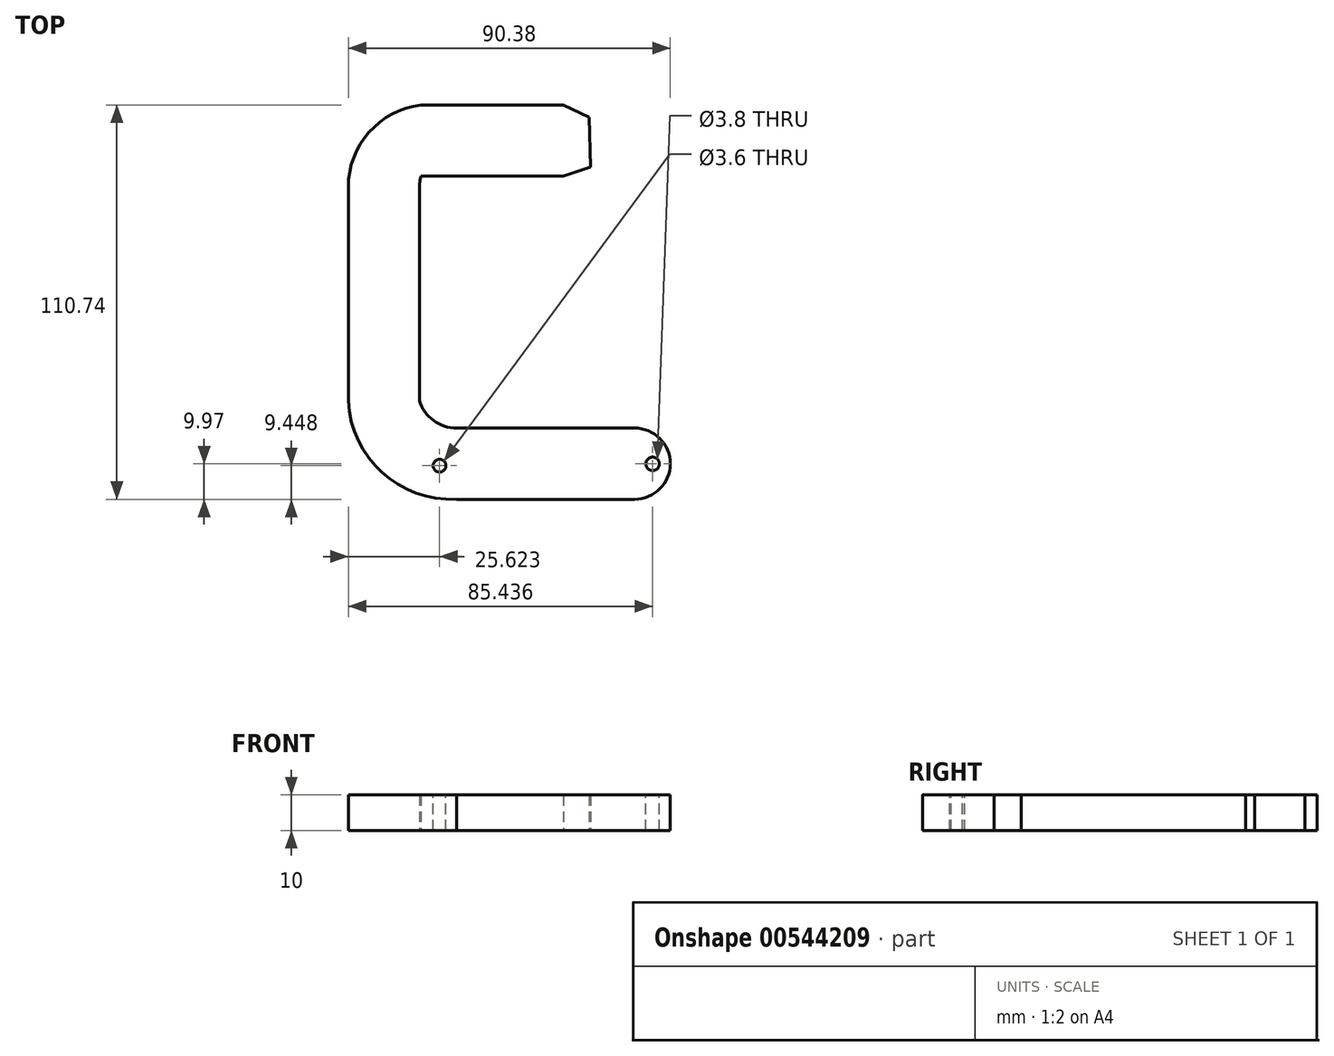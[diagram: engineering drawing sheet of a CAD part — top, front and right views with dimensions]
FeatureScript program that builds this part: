
annotation { "Feature Type Name" : "Feature", "Feature Type Description" : "" }
export const myFeature = defineFeature(function(context is Context, id is Id, definition is map)
    precondition{}
    {
        {
            var Q0;
            Q0=qCreatedBy(makeId("Top.planeOp"),FACE);
            var sketch = newSketch(context, id + "F0", { "sketchPlane" : qUnion([Q0])});
            skLineSegment(sketch, "E0.bottom", {"start": v(20, 10) * mm, "end": v(-30, 10) * mm});
            skLineSegment(sketch, "E0.top", {"start": v(20, -10) * mm, "end": v(-30, -10) * mm});
            skLineSegment(sketch, "E0.left", {"start": v(30, 0) * mm, "end": v(30, 0) * mm});
            skLineSegment(sketch, "E0.right", {"start": v(-30, 10) * mm, "end": v(-30, -10) * mm});
            skPoint(sketch, "E0.middle", {"position": v(0, 0) * mm});
            skLineSegment(sketch, "E1.bottom", {"start": v(-40.38, 77.65) * mm, "end": v(-60.38, 77.65) * mm});
            skLineSegment(sketch, "E1.top", {"start": v(-40.38, 17.65) * mm, "end": v(-60.38, 17.65) * mm});
            skLineSegment(sketch, "E1.left", {"start": v(-40.38, 77.65) * mm, "end": v(-40.38, 17.65) * mm});
            skLineSegment(sketch, "E1.right", {"start": v(-60.38, 77.65) * mm, "end": v(-60.38, 17.65) * mm});
            skArc(sketch, "E2", {"start": v(-40.38, 17.65) * mm, "mid": v(-36.45, 12.12) * mm, "end": v(-30, 10) * mm});
            skArc(sketch, "E3", {"start": v(-60.38, 17.65) * mm, "mid": v(-50.9, -2.45) * mm, "end": v(-30, -10) * mm});
            skLineSegment(sketch, "E4.bottom", {"start": v(-40, 100.71) * mm, "end": v(0, 100.71) * mm});
            skLineSegment(sketch, "E4.top", {"start": v(-40, 80.71) * mm, "end": v(0, 80.71) * mm});
            skLineSegment(sketch, "E4.left", {"start": v(-40, 100.71) * mm, "end": v(-40, 80.71) * mm});
            skLineSegment(sketch, "E4.right", {"start": v(0, 100.71) * mm, "end": v(0, 80.71) * mm});
            skArc(sketch, "E5", {"start": v(-40, 80.71) * mm, "mid": v(-40.29, 79.2) * mm, "end": v(-40.38, 77.65) * mm});
            skArc(sketch, "E6", {"start": v(-40, 100.71) * mm, "mid": v(-54.56, 93.04) * mm, "end": v(-60.38, 77.65) * mm});
            skLineSegment(sketch, "E7", {"start": v(0, 100.71) * mm, "end": v(7.2, 97.23) * mm});
            skLineSegment(sketch, "E8", {"start": v(0, 80.71) * mm, "end": v(7.6, 83.24) * mm});
            skLineSegment(sketch, "E9", {"start": v(7.2, 97.23) * mm, "end": v(7.6, 83.24) * mm});
            skPoint(sketch, "E10.visualSharp", {"position": v(30, 10) * mm});
            skArc(sketch, "E10.filletArc", {"start": v(30, 0) * mm, "mid": v(27.07, 7.07) * mm, "end": v(20, 10) * mm});
            skPoint(sketch, "E11.visualSharp", {"position": v(30, -10) * mm});
            skArc(sketch, "E11.filletArc", {"start": v(20, -10) * mm, "mid": v(27.07, -7.07) * mm, "end": v(30, 0) * mm});
            skSolve(sketch);
        }
        {
            var Q0;
            Q0 = qSketchRegion(id + "F0", true);
            extrude(context, id + "F1", {"entities" : qUnion([Q0]), "endBound" : BoundingType.SYMMETRIC, "depth" : 10 * mm, "offsetDistance" : 25 * mm});
        }
        {
            var Q0;
            Q0=makeQuery(id+"F1.opExtrude","CAP_FACE",FACE,{"disambiguationData":[OSD([sQuery(id+"F0.wireOp",EDGE,"E0.bottom"),sQuery(id+"F0.wireOp",EDGE,"E0.top"),sQuery(id+"F0.wireOp",EDGE,"E0.left"),sQuery(id+"F0.wireOp",EDGE,"E1.left"),sQuery(id+"F0.wireOp",EDGE,"E1.right"),sQuery(id+"F0.wireOp",EDGE,"E2"),sQuery(id+"F0.wireOp",EDGE,"E3"),sQuery(id+"F0.wireOp",EDGE,"E4.bottom"),sQuery(id+"F0.wireOp",EDGE,"E4.top"),sQuery(id+"F0.wireOp",EDGE,"E5"),sQuery(id+"F0.wireOp",EDGE,"E6"),sQuery(id+"F0.wireOp",EDGE,"E7"),sQuery(id+"F0.wireOp",EDGE,"E8"),sQuery(id+"F0.wireOp",EDGE,"E9")])],"isStart":false});
            var sketch = newSketch(context, id + "F2", { "sketchPlane" : qUnion([Q0])});
            skCircle(sketch, "E12", {"center": v(25.06, -0.06) * mm, "radius": 1.9 * mm});
            skPoint(sketch, "E12.centerSnap0", {"position": v(30, 0) * mm});
            skSolve(sketch);
        }
        {
            var Q0;
            Q0 = qSketchRegion(id + "F2", true);
            extrude(context, id + "F3", {"entities" : qUnion([Q0]), "operationType" : NewBodyOperationType.REMOVE, "oppositeDirection" : true, "depth" : 26 * mm, "offsetDistance" : 25 * mm});
        }
        {
            var Q0;
            Q0=makeQuery(id+"F1.opExtrude","CAP_FACE",FACE,{"disambiguationData":[OSD([sQuery(id+"F0.wireOp",EDGE,"E0.bottom"),sQuery(id+"F0.wireOp",EDGE,"E0.top"),sQuery(id+"F0.wireOp",EDGE,"E0.left"),sQuery(id+"F0.wireOp",EDGE,"E1.left"),sQuery(id+"F0.wireOp",EDGE,"E1.right"),sQuery(id+"F0.wireOp",EDGE,"E2"),sQuery(id+"F0.wireOp",EDGE,"E3"),sQuery(id+"F0.wireOp",EDGE,"E4.bottom"),sQuery(id+"F0.wireOp",EDGE,"E4.top"),sQuery(id+"F0.wireOp",EDGE,"E5"),sQuery(id+"F0.wireOp",EDGE,"E6"),sQuery(id+"F0.wireOp",EDGE,"E7"),sQuery(id+"F0.wireOp",EDGE,"E8"),sQuery(id+"F0.wireOp",EDGE,"E9")])],"isStart":false});
            var sketch = newSketch(context, id + "F4", { "sketchPlane" : qUnion([Q0])});
            skCircle(sketch, "E13", {"center": v(-34.76, -0.58) * mm, "radius": 1.8 * mm});
            skSolve(sketch);
        }
        {
            var Q0;
            Q0 = qSketchRegion(id + "F4", true);
            extrude(context, id + "F5", {"entities" : qUnion([Q0]), "operationType" : NewBodyOperationType.REMOVE, "oppositeDirection" : true, "depth" : 25 * mm, "offsetDistance" : 25 * mm});
        }
    });
